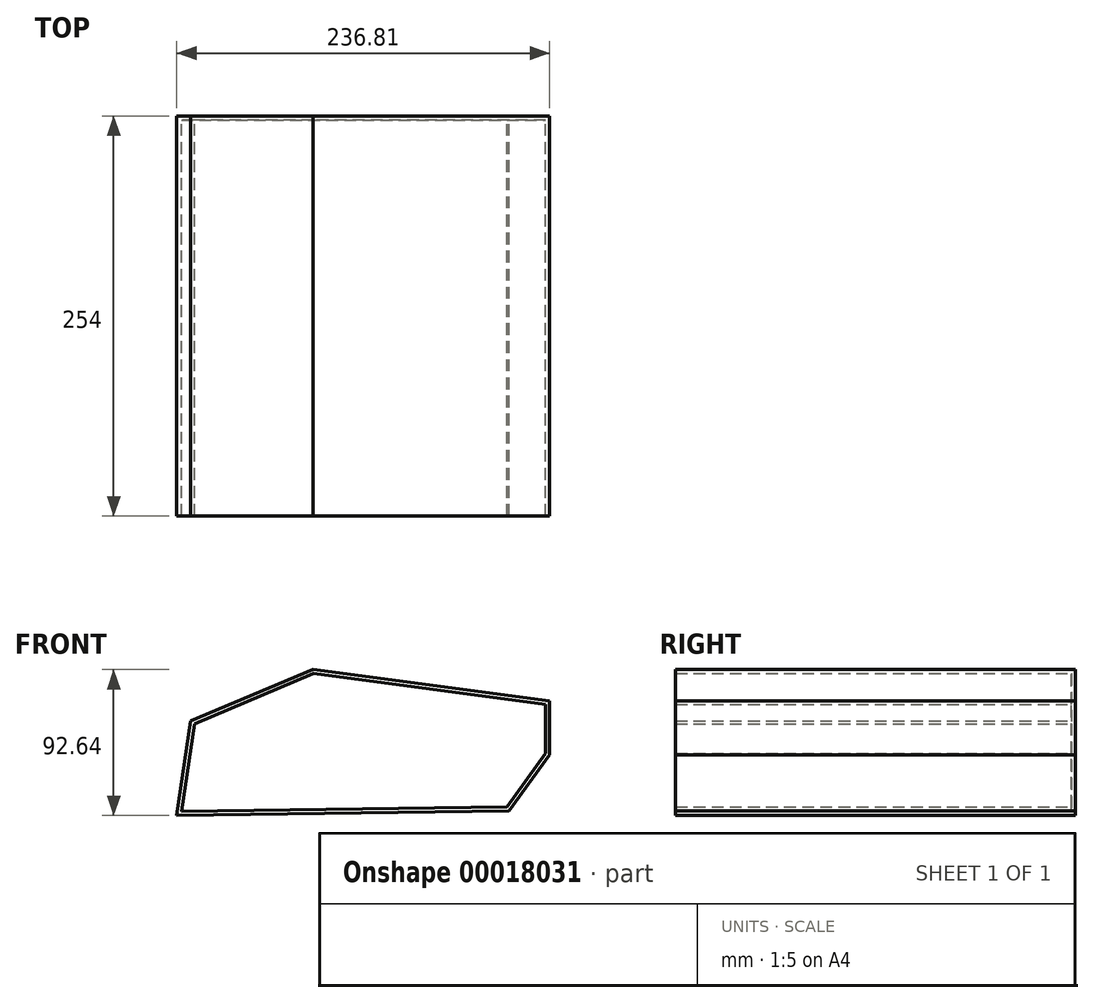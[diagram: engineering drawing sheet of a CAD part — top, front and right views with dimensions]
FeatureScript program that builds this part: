
annotation { "Feature Type Name" : "Feature", "Feature Type Description" : "" }
export const myFeature = defineFeature(function(context is Context, id is Id, definition is map)
    precondition{}
    {
        {
            var Q0;
            Q0=qCreatedBy(makeId("Front.planeOp"),FACE);
            var sketch = newSketch(context, id + "F0", { "sketchPlane" : qUnion([Q0])});
            skLineSegment(sketch, "E0", {"start": v(-101.16, -2.83) * mm, "end": v(109.78, 0) * mm});
            skLineSegment(sketch, "E1", {"start": v(109.78, 0) * mm, "end": v(135.65, 35.68) * mm});
            skLineSegment(sketch, "E2", {"start": v(135.65, 35.68) * mm, "end": v(135.65, 69.93) * mm});
            skLineSegment(sketch, "E3", {"start": v(135.65, 69.93) * mm, "end": v(-14.6, 89.81) * mm});
            skLineSegment(sketch, "E4", {"start": v(-14.6, 89.81) * mm, "end": v(-92.2, 57.13) * mm});
            skLineSegment(sketch, "E5", {"start": v(-92.2, 57.13) * mm, "end": v(-101.16, -2.83) * mm});
            skSolve(sketch);
        }
        {
            var Q0;
            Q0=makeQuery(id+"F0.imprint","IMPRINT",FACE,{"disambiguationData":[TD([[makeQuery(id+"F0.imprint","IMPRINT",EDGE,{"derivedFrom":sQuery(id+"F0.wireOp",EDGE,"E0")}),1.0]])]});
            extrude(context, id + "F1", {"entities" : qUnion([Q0]), "depth" : 254 * mm});
        }
        {
            var Q0;
            Q0=makeQuery(id+"F1.opExtrude","CAP_FACE",FACE,{"disambiguationData":[OSD([sQuery(id+"F0.wireOp",EDGE,"E0"),sQuery(id+"F0.wireOp",EDGE,"E1"),sQuery(id+"F0.wireOp",EDGE,"E2"),sQuery(id+"F0.wireOp",EDGE,"E3"),sQuery(id+"F0.wireOp",EDGE,"E4"),sQuery(id+"F0.wireOp",EDGE,"E5")])],"isStart":false});
            shell(context, id + "F2", {"entities" : qUnion([Q0]), "thickness" : 2.54 * mm});
        }
    });
